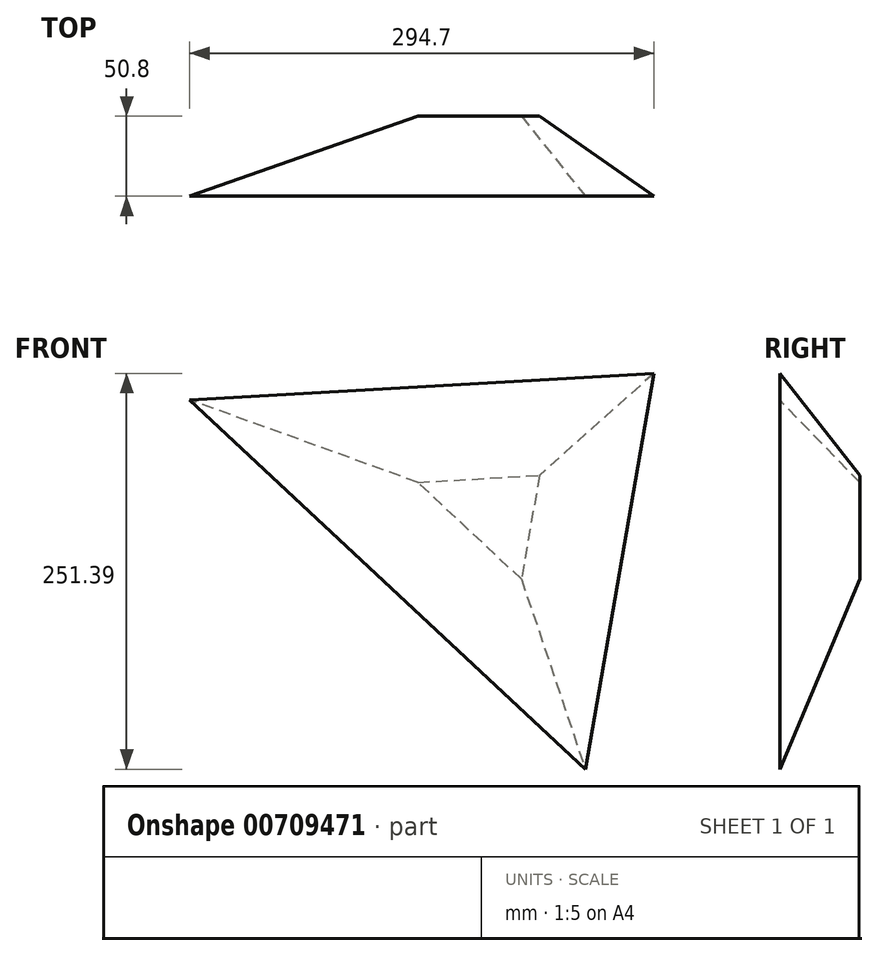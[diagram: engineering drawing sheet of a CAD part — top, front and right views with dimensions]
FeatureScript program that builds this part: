
annotation { "Feature Type Name" : "Feature", "Feature Type Description" : "" }
export const myFeature = defineFeature(function(context is Context, id is Id, definition is map)
    precondition{}
    {
        {
            var Q0;
            Q0=qCreatedBy(makeId("Front.planeOp"),FACE);
            var sketch = newSketch(context, id + "F0", { "sketchPlane" : qUnion([Q0])});
            skLineSegment(sketch, "E0", {"start": v(-57.53, 42.95) * mm, "end": v(19.72, 47.37) * mm});
            skLineSegment(sketch, "E1", {"start": v(19.72, 47.37) * mm, "end": v(8.33, -18.53) * mm});
            skLineSegment(sketch, "E2", {"start": v(-57.53, 42.95) * mm, "end": v(8.33, -18.53) * mm});
            skSolve(sketch);
        }
        {
            var Q0;
            Q0 = qSketchRegion(id + "F0", true);
            extrude(context, id + "F1", {"entities" : qUnion([Q0]), "depth" : 50.8 * mm, "offsetDistance" : 25.4 * mm, "hasDraft" : true, "draftAngle" : 50 * degree});
        }
    });
